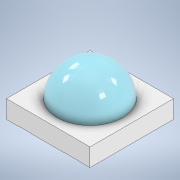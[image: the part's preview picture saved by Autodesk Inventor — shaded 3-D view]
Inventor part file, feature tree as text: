
AUTODESK INVENTOR PART (.ipt)
format: ipt  version: 2020.2 (Build 242310000, 310)  size: 182,272 bytes
history: native  units: mm
features: extrude x3, sketch x3, fillet x1
ambient origin geometry x8: Origin, YZ Plane, XZ Plane, XY Plane, X Axis, Y Axis, Z Axis, Center Point
bodies: Body1 (feature_tree)
feature tree (7):
  extrude  "Extrusion2"  Depth=3.3mm
  sketch  "Skizze5"  dims[d12=1.3mm d13=1.3mm d14=3.3mm d15=0.5mm d16=3.3mm d19=1.4mm d20=0.5mm d21=3.3mm d22=1.4mm d26=0.5mm d27=0.05mm d28=1.4mm d31=0.01mm d32=0.0mm]
  extrude  "Extrusion3"  Depth=1.3mm
  fillet  "Rundung1"  Radius=1.3mm
  extrude  "Extrusion5"  Depth=1.3mm
  sketch  "Skizze3"  dims[d5=3.3mm d6=3.3mm]
  sketch  "Skizze4"  dims[d7=0.7mm d8=0.0mm d9=2.6mm d10=1.3mm d11=0.0mm]
